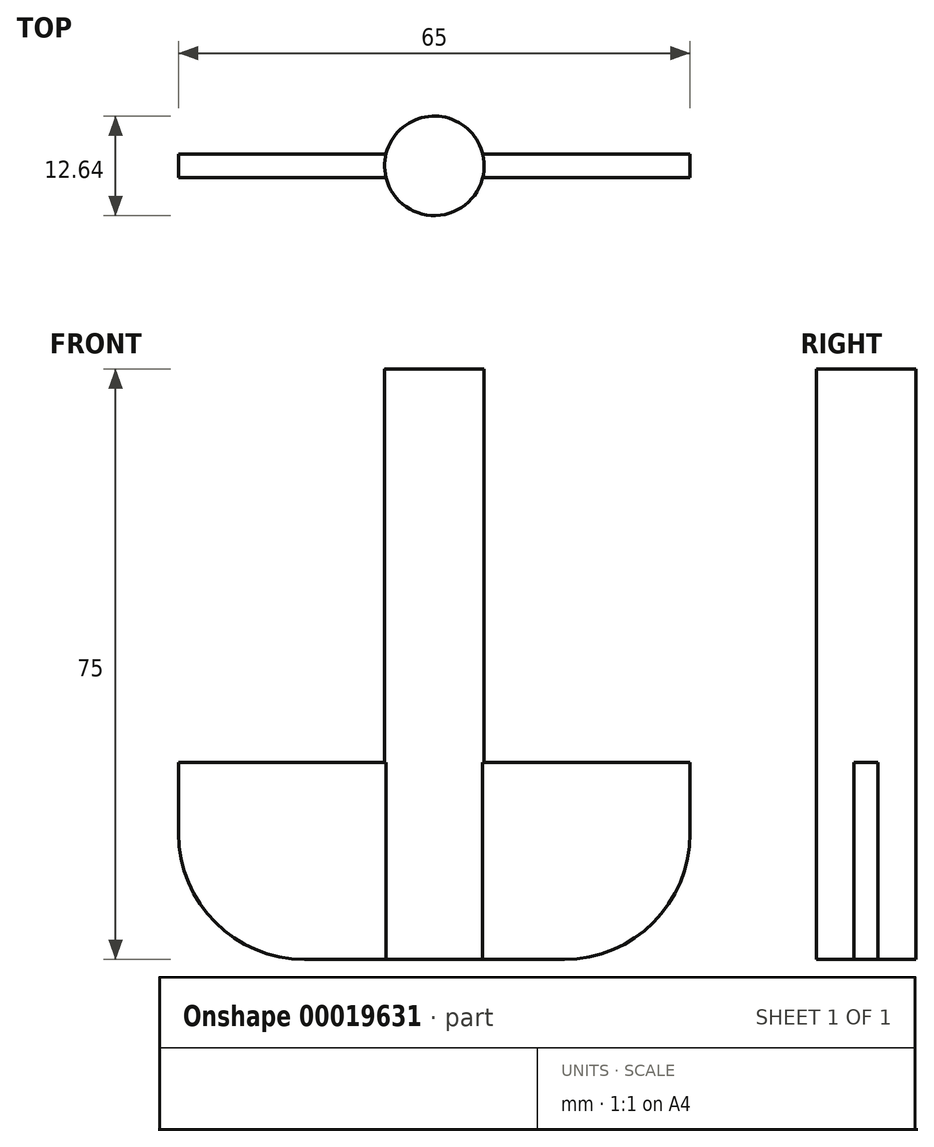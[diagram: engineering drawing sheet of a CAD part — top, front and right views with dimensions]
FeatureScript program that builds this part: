
annotation { "Feature Type Name" : "Feature", "Feature Type Description" : "" }
export const myFeature = defineFeature(function(context is Context, id is Id, definition is map)
    precondition{}
    {
        {
            var Q0;
            Q0=qCreatedBy(makeId("Top.planeOp"),FACE);
            var sketch = newSketch(context, id + "F0", { "sketchPlane" : qUnion([Q0])});
            skCircle(sketch, "E0", {"center": v(0, 0) * mm, "radius": 6.32 * mm});
            skSolve(sketch);
        }
        {
            var Q0;
            Q0=makeQuery(id+"F0.imprint","IMPRINT",FACE,{"disambiguationData":[TD([[makeQuery(id+"F0.imprint","IMPRINT",EDGE,{"derivedFrom":sQuery(id+"F0.wireOp",EDGE,"E0")}),1.0]])]});
            extrude(context, id + "F1", {"entities" : qUnion([Q0]), "depth" : 75 * mm});
        }
        {
            var Q0;
            Q0=makeQuery(id+"F1.opExtrude","CAP_FACE",FACE,{"disambiguationData":[OSD([sQuery(id+"F0.wireOp",EDGE,"E0")])],"isStart":true});
            var sketch = newSketch(context, id + "F2", { "sketchPlane" : qUnion([Q0])});
            skLineSegment(sketch, "E1.bottom", {"start": v(-6.32, -1.5) * mm, "end": v(6.32, -1.5) * mm});
            skLineSegment(sketch, "E1.top", {"start": v(-6.32, 1.5) * mm, "end": v(6.32, 1.5) * mm});
            skLineSegment(sketch, "E1.left", {"start": v(-6.32, -1.5) * mm, "end": v(-6.32, 1.5) * mm});
            skLineSegment(sketch, "E1.right", {"start": v(6.32, -1.5) * mm, "end": v(6.32, 1.5) * mm});
            skCircle(sketch, "E2.0", {"center": v(0, 0) * mm, "radius": 6.32 * mm});
            skSolve(sketch);
        }
        {
            var Q0;
            {var subQ0=sQuery(id+"F2.wireOp",EDGE,"E2.0");var subQ6=sQuery(id+"F2.wireOp",EDGE,"E1.bottom");var subQ7=makeQuery(id+"F2.imprint","INTERSECT",VERTEX,{"disambiguationData":[OD(0.0)],"derivedFrom":[subQ6,subQ0]});Q0=makeQuery(id+"F2.imprint","IMPRINT",FACE,{"disambiguationData":[TD([[makeQuery(id+"F2.imprint","IMPRINT",EDGE,{"disambiguationData":[TD([[subQ7,-1.0]])],"derivedFrom":subQ6}),1.0]])]});}
            extrude(context, id + "F3", {"entities" : qUnion([Q0]), "operationType" : NewBodyOperationType.REMOVE, "oppositeDirection" : true, "depth" : 25 * mm});
        }
        {
            var Q0;
            Q0=makeQuery(id+"F3.boolean.opBoolean","COPY",FACE,{"derivedFrom":makeQuery(id+"F3.opExtrude","SWEPT_FACE",FACE,{"disambiguationData":[OSD([sQuery(id+"F2.wireOp",EDGE,"E1.bottom")])]})});
            var sketch = newSketch(context, id + "F4", { "sketchPlane" : qUnion([Q0])});
            skLineSegment(sketch, "E3.0", {"start": v(-6.14, 25) * mm, "end": v(-6.14, 0) * mm});
            skLineSegment(sketch, "E4.0", {"start": v(-6.14, 0) * mm, "end": v(6.14, 0) * mm});
            skLineSegment(sketch, "E5.bottom", {"start": v(-32.5, 0) * mm, "end": v(32.5, 0) * mm});
            skLineSegment(sketch, "E5.top", {"start": v(-32.5, 25) * mm, "end": v(32.5, 25) * mm});
            skLineSegment(sketch, "E5.left", {"start": v(-32.5, 0) * mm, "end": v(-32.5, 25) * mm});
            skLineSegment(sketch, "E5.right", {"start": v(32.5, 0) * mm, "end": v(32.5, 25) * mm});
            skSolve(sketch);
        }
        {
            var Q0;
            {var subQ3=sQuery(id+"F4.wireOp",EDGE,"E5.right");Q0=makeQuery(id+"F4.imprint","IMPRINT",FACE,{"disambiguationData":[TD([[makeQuery(id+"F4.imprint","IMPRINT",EDGE,{"derivedFrom":subQ3}),1.0]])]});}
            var Q1;
            {var subQ2=sQuery(id+"F4.wireOp",EDGE,"E3.0");Q1=makeQuery(id+"F4.imprint","IMPRINT",FACE,{"disambiguationData":[TD([[makeQuery(id+"F4.imprint","IMPRINT",EDGE,{"derivedFrom":subQ2}),-1.0]])]});}
            var Q2;
            {var subQ4=sQuery(id+"F4.wireOp",EDGE,"E3.0");Q2=makeQuery(id+"F4.imprint","IMPRINT",FACE,{"disambiguationData":[TD([[makeQuery(id+"F4.imprint","IMPRINT",EDGE,{"derivedFrom":subQ4}),1.0]])]});}
            extrude(context, id + "F5", {"entities" : qUnion([Q0, Q1, Q2]), "operationType" : NewBodyOperationType.ADD, "depth" : 3 * mm});
        }
        {
            var Q0;
            Q0=makeQuery(id+"F5.opExtrude","SWEPT_EDGE",EDGE,{"disambiguationData":[OSD([sQuery(id+"F4.wireOp",EDGE,"E5.bottom"),sQuery(id+"F4.wireOp",EDGE,"E5.left")])]});
            var Q1;
            Q1=makeQuery(id+"F5.opExtrude","SWEPT_EDGE",EDGE,{"disambiguationData":[OSD([sQuery(id+"F4.wireOp",EDGE,"E5.bottom"),sQuery(id+"F4.wireOp",EDGE,"E5.right")])]});
            fillet(context, id + "F6", {"entities" : qUnion([Q0, Q1]), "radius" : 16 * mm, "tangentPropagation" : true, "allowEdgeOverflow" : false});
        }
    });
